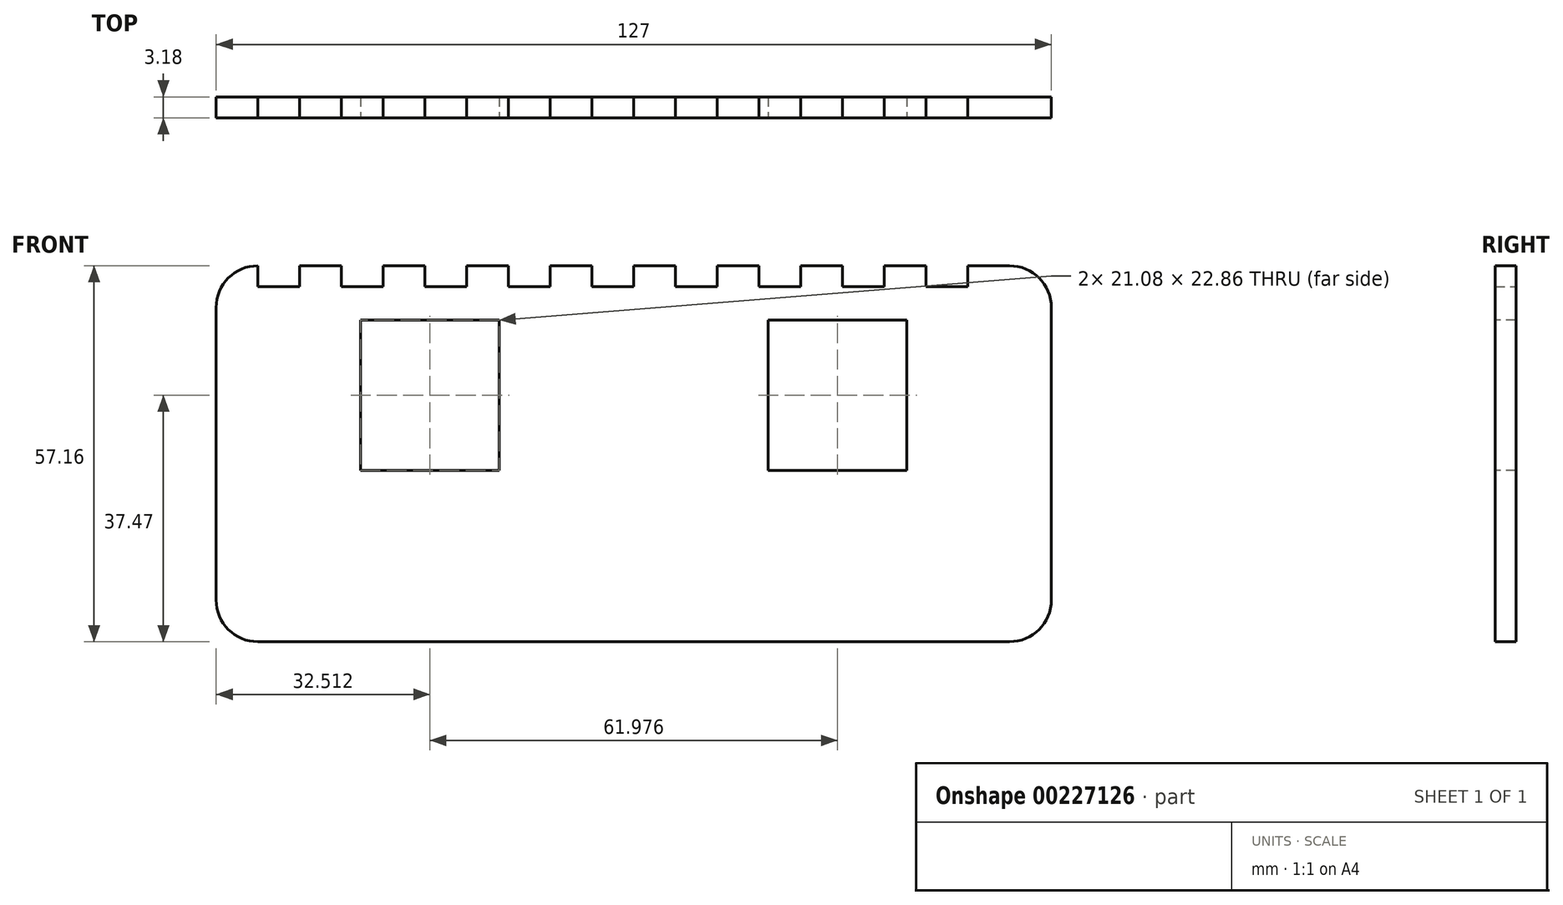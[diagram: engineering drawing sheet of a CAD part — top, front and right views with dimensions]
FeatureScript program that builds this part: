
annotation { "Feature Type Name" : "Feature", "Feature Type Description" : "" }
export const myFeature = defineFeature(function(context is Context, id is Id, definition is map)
    precondition{}
    {
        {
            var Q0;
            Q0=qCreatedBy(makeId("Front.planeOp"),FACE);
            var sketch = newSketch(context, id + "F0", { "sketchPlane" : qUnion([Q0])});
            skLineSegment(sketch, "E0.bottom", {"start": v(57.15, 28.58) * mm, "end": v(50.8, 28.58) * mm});
            skLineSegment(sketch, "E0.top", {"start": v(57.15, -28.58) * mm, "end": v(-57.15, -28.58) * mm});
            skLineSegment(sketch, "E0.left", {"start": v(63.5, 22.22) * mm, "end": v(63.5, -22.22) * mm});
            skLineSegment(sketch, "E0.right", {"start": v(-63.5, 22.22) * mm, "end": v(-63.5, -22.22) * mm});
            skPoint(sketch, "E0.middle", {"position": v(0, 0) * mm});
            skPoint(sketch, "E1.visualSharp", {"position": v(-63.5, 28.58) * mm});
            skArc(sketch, "E1.filletArc", {"start": v(-57.15, 28.58) * mm, "mid": v(-61.64, 26.72) * mm, "end": v(-63.5, 22.22) * mm});
            skPoint(sketch, "E2.visualSharp", {"position": v(-63.5, -28.58) * mm});
            skArc(sketch, "E2.filletArc", {"start": v(-63.5, -22.22) * mm, "mid": v(-61.64, -26.72) * mm, "end": v(-57.15, -28.57) * mm});
            skPoint(sketch, "E3.visualSharp", {"position": v(63.5, -28.58) * mm});
            skArc(sketch, "E3.filletArc", {"start": v(57.15, -28.58) * mm, "mid": v(61.64, -26.72) * mm, "end": v(63.5, -22.22) * mm});
            skPoint(sketch, "E4.visualSharp", {"position": v(63.5, 28.58) * mm});
            skArc(sketch, "E4.filletArc", {"start": v(63.5, 22.22) * mm, "mid": v(61.64, 26.72) * mm, "end": v(57.15, 28.58) * mm});
            skLineSegment(sketch, "E5.top", {"start": v(-57.15, 25.4) * mm, "end": v(-50.8, 25.4) * mm});
            skLineSegment(sketch, "E5.left", {"start": v(-57.15, 28.58) * mm, "end": v(-57.15, 25.4) * mm});
            skLineSegment(sketch, "E5.right", {"start": v(-50.8, 28.58) * mm, "end": v(-50.8, 25.4) * mm});
            skLineSegment(sketch, "E6.1.0.2", {"start": v(-44.45, 28.58) * mm, "end": v(-44.45, 25.4) * mm});
            skLineSegment(sketch, "E6.2.0.0", {"start": v(-44.45, 25.4) * mm, "end": v(-38.1, 25.4) * mm});
            skLineSegment(sketch, "E6.2.0.1", {"start": v(-44.45, 28.58) * mm, "end": v(-44.45, 25.4) * mm});
            skLineSegment(sketch, "E6.2.0.2", {"start": v(-38.1, 28.58) * mm, "end": v(-38.1, 25.4) * mm});
            skLineSegment(sketch, "E6.direction1", {"start": v(-57.15, 25.4) * mm, "end": v(-50.8, 25.4) * mm, "construction": true});
            skLineSegment(sketch, "E6.direction2", {"start": v(-57.15, 25.4) * mm, "end": v(-57.15, 5.59) * mm, "construction": true});
            skLineSegment(sketch, "E7.6.3.0", {"start": v(-31.75, 28.58) * mm, "end": v(-31.75, 25.4) * mm});
            skLineSegment(sketch, "E7.0.4.0", {"start": v(-31.75, 25.4) * mm, "end": v(-25.4, 25.4) * mm});
            skLineSegment(sketch, "E7.3.4.0", {"start": v(-31.75, 28.58) * mm, "end": v(-31.75, 25.4) * mm});
            skLineSegment(sketch, "E7.6.4.0", {"start": v(-25.4, 28.58) * mm, "end": v(-25.4, 25.4) * mm});
            skLineSegment(sketch, "E7.3.5.0", {"start": v(-25.4, 28.58) * mm, "end": v(-25.4, 25.4) * mm});
            skLineSegment(sketch, "E7.6.5.0", {"start": v(-19.05, 28.58) * mm, "end": v(-19.05, 25.4) * mm});
            skLineSegment(sketch, "E7.0.6.0", {"start": v(-19.05, 25.4) * mm, "end": v(-12.7, 25.4) * mm});
            skLineSegment(sketch, "E7.3.6.0", {"start": v(-19.05, 28.58) * mm, "end": v(-19.05, 25.4) * mm});
            skLineSegment(sketch, "E7.6.6.0", {"start": v(-12.7, 28.58) * mm, "end": v(-12.7, 25.4) * mm});
            skLineSegment(sketch, "E7.3.7.0", {"start": v(-12.7, 28.58) * mm, "end": v(-12.7, 25.4) * mm});
            skLineSegment(sketch, "E7.6.7.0", {"start": v(-6.35, 28.58) * mm, "end": v(-6.35, 25.4) * mm});
            skLineSegment(sketch, "E7.0.8.0", {"start": v(-6.35, 25.4) * mm, "end": v(0, 25.4) * mm});
            skLineSegment(sketch, "E7.3.8.0", {"start": v(-6.35, 28.58) * mm, "end": v(-6.35, 25.4) * mm});
            skLineSegment(sketch, "E7.6.8.0", {"start": v(0, 28.58) * mm, "end": v(0, 25.4) * mm});
            skLineSegment(sketch, "E7.3.9.0", {"start": v(0, 28.58) * mm, "end": v(0, 25.4) * mm});
            skLineSegment(sketch, "E7.6.9.0", {"start": v(6.35, 28.58) * mm, "end": v(6.35, 25.4) * mm});
            skLineSegment(sketch, "E7.0.10.0", {"start": v(6.35, 25.4) * mm, "end": v(12.7, 25.4) * mm});
            skLineSegment(sketch, "E7.3.10.0", {"start": v(6.35, 28.58) * mm, "end": v(6.35, 25.4) * mm});
            skLineSegment(sketch, "E7.6.10.0", {"start": v(12.7, 28.58) * mm, "end": v(12.7, 25.4) * mm});
            skLineSegment(sketch, "E7.3.11.0", {"start": v(12.7, 28.58) * mm, "end": v(12.7, 25.4) * mm});
            skLineSegment(sketch, "E7.6.11.0", {"start": v(19.05, 28.58) * mm, "end": v(19.05, 25.4) * mm});
            skLineSegment(sketch, "E7.0.12.0", {"start": v(19.05, 25.4) * mm, "end": v(25.4, 25.4) * mm});
            skLineSegment(sketch, "E7.3.12.0", {"start": v(19.05, 28.58) * mm, "end": v(19.05, 25.4) * mm});
            skLineSegment(sketch, "E7.6.12.0", {"start": v(25.4, 28.58) * mm, "end": v(25.4, 25.4) * mm});
            skLineSegment(sketch, "E7.3.13.0", {"start": v(25.4, 28.58) * mm, "end": v(25.4, 25.4) * mm});
            skLineSegment(sketch, "E7.6.13.0", {"start": v(31.75, 28.58) * mm, "end": v(31.75, 25.4) * mm});
            skLineSegment(sketch, "E7.0.14.0", {"start": v(31.75, 25.4) * mm, "end": v(38.1, 25.4) * mm});
            skLineSegment(sketch, "E7.3.14.0", {"start": v(31.75, 28.58) * mm, "end": v(31.75, 25.4) * mm});
            skLineSegment(sketch, "E7.6.14.0", {"start": v(38.1, 28.58) * mm, "end": v(38.1, 25.4) * mm});
            skLineSegment(sketch, "E7.3.15.0", {"start": v(38.1, 28.58) * mm, "end": v(38.1, 25.4) * mm});
            skLineSegment(sketch, "E7.6.15.0", {"start": v(44.45, 28.58) * mm, "end": v(44.45, 25.4) * mm});
            skLineSegment(sketch, "E7.0.16.0", {"start": v(44.45, 25.4) * mm, "end": v(50.8, 25.4) * mm});
            skLineSegment(sketch, "E7.3.16.0", {"start": v(44.45, 28.58) * mm, "end": v(44.45, 25.4) * mm});
            skLineSegment(sketch, "E7.6.16.0", {"start": v(50.8, 28.58) * mm, "end": v(50.8, 25.4) * mm});
            skLineSegment(sketch, "E7.3.17.0", {"start": v(50.8, 28.58) * mm, "end": v(50.8, 25.4) * mm});
            skLineSegment(sketch, "E8.trimOffspring", {"start": v(-44.45, 28.58) * mm, "end": v(-50.8, 28.58) * mm});
            skLineSegment(sketch, "E9.trimOffspring", {"start": v(-31.75, 28.58) * mm, "end": v(-38.1, 28.58) * mm});
            skLineSegment(sketch, "E10.trimOffspring", {"start": v(-19.05, 28.58) * mm, "end": v(-25.4, 28.58) * mm});
            skLineSegment(sketch, "E11.trimOffspring", {"start": v(-6.35, 28.58) * mm, "end": v(-12.7, 28.58) * mm});
            skLineSegment(sketch, "E12.trimOffspring", {"start": v(6.35, 28.58) * mm, "end": v(0, 28.58) * mm});
            skLineSegment(sketch, "E13.trimOffspring", {"start": v(19.05, 28.58) * mm, "end": v(12.7, 28.58) * mm});
            skLineSegment(sketch, "E14.trimOffspring", {"start": v(31.75, 28.58) * mm, "end": v(25.4, 28.58) * mm});
            skLineSegment(sketch, "E15.trimOffspring", {"start": v(44.45, 28.58) * mm, "end": v(38.1, 28.58) * mm});
            skSolve(sketch);
        }
        {
            var Q0;
            Q0=makeQuery(id+"F0.imprint","IMPRINT",FACE,{"disambiguationData":[TD([[makeQuery(id+"F0.imprint","IMPRINT",EDGE,{"derivedFrom":sQuery(id+"F0.wireOp",EDGE,"E0.bottom")}),1.0]])]});
            extrude(context, id + "F1", {"entities" : qUnion([Q0]), "depth" : 3.17 * mm, "offsetDistance" : 25.4 * mm});
        }
        {
            var Q0;
            Q0=makeQuery(id+"F1.opExtrude","CAP_FACE",FACE,{"disambiguationData":[OSD([sQuery(id+"F0.wireOp",EDGE,"E0.bottom"),sQuery(id+"F0.wireOp",EDGE,"E0.top"),sQuery(id+"F0.wireOp",EDGE,"E0.left"),sQuery(id+"F0.wireOp",EDGE,"E0.right")])],"isStart":false});
            var sketch = newSketch(context, id + "F2", { "sketchPlane" : qUnion([Q0])});
            skLineSegment(sketch, "E16.bottom", {"start": v(-60.32, 25.4) * mm, "end": v(60.33, 25.4) * mm, "construction": true});
            skLineSegment(sketch, "E16.top", {"start": v(-60.33, -25.4) * mm, "end": v(60.32, -25.4) * mm, "construction": true});
            skLineSegment(sketch, "E16.left", {"start": v(-60.32, 25.4) * mm, "end": v(-60.33, -25.4) * mm, "construction": true});
            skLineSegment(sketch, "E16.right", {"start": v(60.33, 25.4) * mm, "end": v(60.32, -25.4) * mm, "construction": true});
            skPoint(sketch, "E16.middle", {"position": v(0, 0) * mm});
            skLineSegment(sketch, "E17", {"start": v(0, -25.4) * mm, "end": v(0, -2.54) * mm, "construction": true});
            skLineSegment(sketch, "E18", {"start": v(0, -2.54) * mm, "end": v(0, 20.32) * mm, "construction": true});
            skLineSegment(sketch, "E19", {"start": v(0, 20.32) * mm, "end": v(60.33, 20.32) * mm});
            skLineSegment(sketch, "E20", {"start": v(0, 20.32) * mm, "end": v(-60.33, 20.32) * mm});
            skLineSegment(sketch, "E21", {"start": v(0, -2.54) * mm, "end": v(60.33, -2.54) * mm});
            skLineSegment(sketch, "E22", {"start": v(0, -2.54) * mm, "end": v(-60.33, -2.54) * mm});
            skLineSegment(sketch, "E23.bottom", {"start": v(10.29, 20.32) * mm, "end": v(-10.29, 20.32) * mm});
            skLineSegment(sketch, "E23.top", {"start": v(10.29, -2.54) * mm, "end": v(-10.29, -2.54) * mm});
            skLineSegment(sketch, "E23.left", {"start": v(10.29, 20.32) * mm, "end": v(10.29, -2.54) * mm});
            skLineSegment(sketch, "E23.right", {"start": v(-10.29, 20.32) * mm, "end": v(-10.29, -2.54) * mm});
            skPoint(sketch, "E23.middle", {"position": v(0, 8.89) * mm});
            skLineSegment(sketch, "E24", {"start": v(10.29, 8.89) * mm, "end": v(20.45, 8.89) * mm, "construction": true});
            skLineSegment(sketch, "E25", {"start": v(-10.29, 8.89) * mm, "end": v(-20.45, 8.9) * mm, "construction": true});
            skLineSegment(sketch, "E26", {"start": v(-20.45, 20.32) * mm, "end": v(-20.45, -2.54) * mm});
            skLineSegment(sketch, "E27", {"start": v(20.45, 20.32) * mm, "end": v(20.45, -2.54) * mm});
            skLineSegment(sketch, "E28", {"start": v(-20.45, -2.54) * mm, "end": v(-41.53, -2.54) * mm, "construction": true});
            skLineSegment(sketch, "E29", {"start": v(-41.53, -2.54) * mm, "end": v(-41.53, 20.32) * mm});
            skLineSegment(sketch, "E30", {"start": v(20.45, -2.54) * mm, "end": v(41.53, -2.54) * mm, "construction": true});
            skLineSegment(sketch, "E31", {"start": v(41.53, -2.54) * mm, "end": v(41.53, 20.32) * mm});
            skSolve(sketch);
        }
        {
            var Q0;
            {var subQ0=sQuery(id+"F2.wireOp",EDGE,"E26");Q0=makeQuery(id+"F2.imprint","IMPRINT",FACE,{"disambiguationData":[TD([[makeQuery(id+"F2.imprint","IMPRINT",EDGE,{"derivedFrom":subQ0}),-1.0]])]});}
            var Q1;
            Q1=makeQuery(id+"F2.imprint","IMPRINT",FACE,{"disambiguationData":[TD([[makeQuery(id+"F2.imprint","IMPRINT",EDGE,{"derivedFrom":sQuery(id+"F2.wireOp",EDGE,"E23.bottom")}),1.0]])]});
            var Q2;
            {var subQ0=sQuery(id+"F2.wireOp",EDGE,"E27");Q2=makeQuery(id+"F2.imprint","IMPRINT",FACE,{"disambiguationData":[TD([[makeQuery(id+"F2.imprint","IMPRINT",EDGE,{"derivedFrom":subQ0}),1.0]])]});}
            extrude(context, id + "F3", {"entities" : qUnion([Q0, Q1, Q2]), "operationType" : NewBodyOperationType.REMOVE, "oppositeDirection" : true, "depth" : 25.4 * mm, "offsetDistance" : 25.4 * mm});
        }
    });
